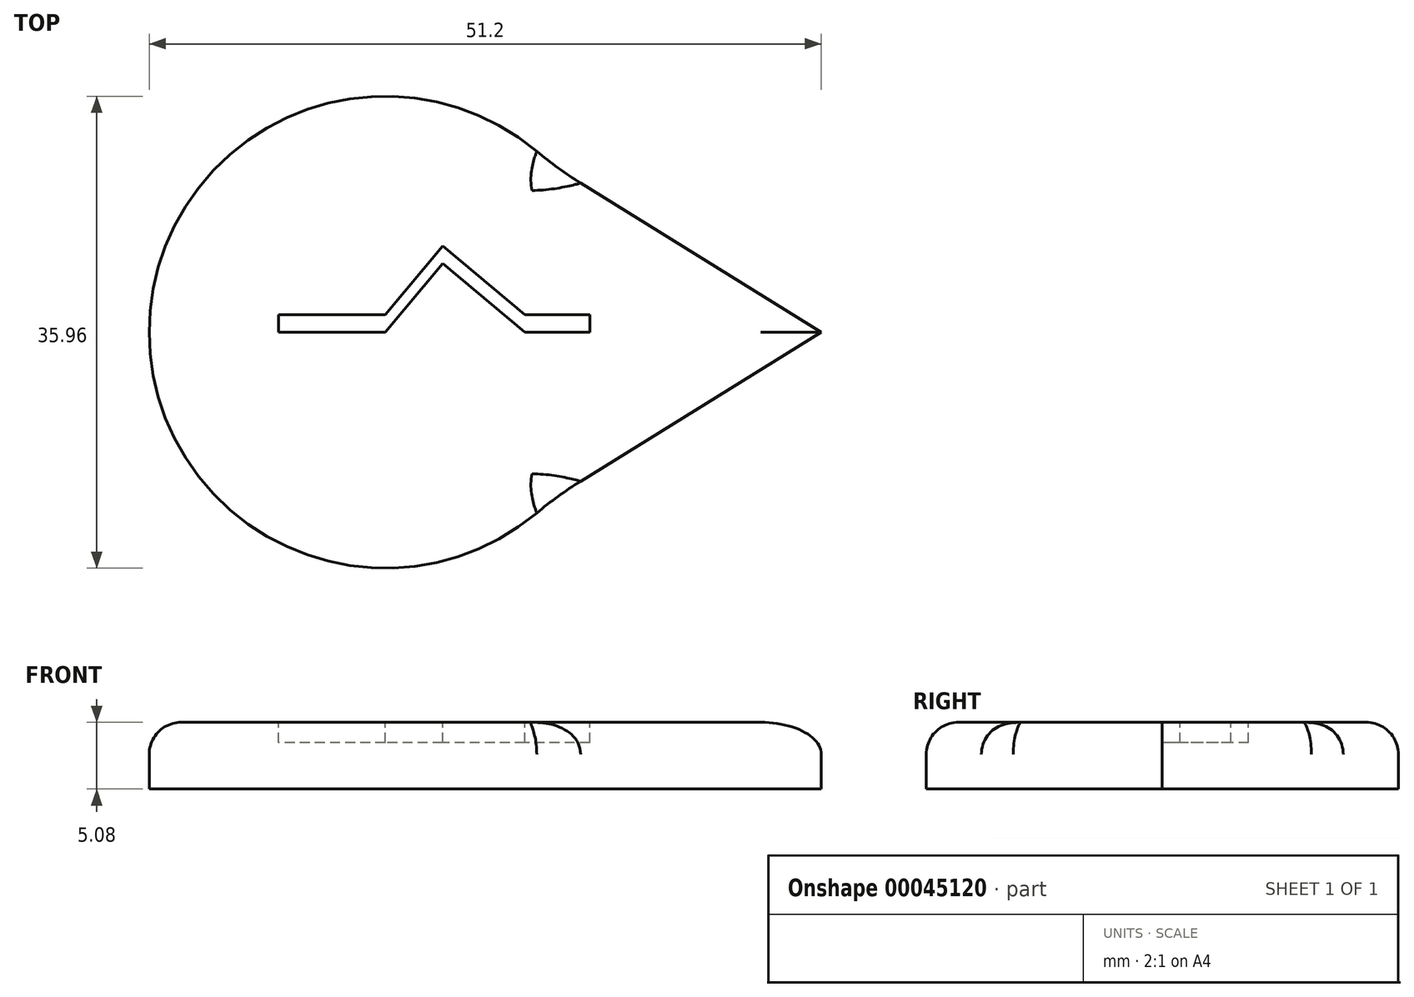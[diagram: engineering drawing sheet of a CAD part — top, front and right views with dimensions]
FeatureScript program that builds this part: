
annotation { "Feature Type Name" : "Feature", "Feature Type Description" : "" }
export const myFeature = defineFeature(function(context is Context, id is Id, definition is map)
    precondition{}
    {
        {
            var Q0;
            Q0=qCreatedBy(makeId("Top.planeOp"),FACE);
            var sketch = newSketch(context, id + "F0", { "sketchPlane" : qUnion([Q0])});
            skCircle(sketch, "E0", {"center": v(0, 0) * mm, "radius": 17.98 * mm});
            skLineSegment(sketch, "E1", {"start": v(-17.98, 0) * mm, "end": v(17.98, 0) * mm});
            skLineSegment(sketch, "E2", {"start": v(0, 0) * mm, "end": v(12.71, 12.71) * mm});
            skLineSegment(sketch, "E3", {"start": v(0, 0) * mm, "end": v(12.71, -12.71) * mm});
            skLineSegment(sketch, "E4", {"start": v(17.98, 0) * mm, "end": v(33.22, 0) * mm});
            skLineSegment(sketch, "E5", {"start": v(12.71, 12.71) * mm, "end": v(33.22, 0) * mm});
            skLineSegment(sketch, "E6", {"start": v(12.71, -12.71) * mm, "end": v(33.22, 0) * mm});
            skSolve(sketch);
        }
        {
            var Q0;
            Q0 = qSketchRegion(id + "F0", true);
            extrude(context, id + "F1", {"entities" : qUnion([Q0]), "depth" : 5.08 * mm});
        }
        {
            var Q0;
            Q0=makeQuery(id+"F1.opExtrude","CAP_EDGE",EDGE,{"disambiguationData":[OSD([sQuery(id+"F0.wireOp",EDGE,"E0")])],"isStart":false});
            var Q1;
            Q1=makeQuery(id+"F1.opExtrude","CAP_EDGE",EDGE,{"disambiguationData":[OSD([sQuery(id+"F0.wireOp",EDGE,"E6")])],"isStart":false});
            var Q2;
            Q2=makeQuery(id+"F1.opExtrude","CAP_EDGE",EDGE,{"disambiguationData":[OSD([sQuery(id+"F0.wireOp",EDGE,"E5")])],"isStart":false});
            fillet(context, id + "F2", {"entities" : qUnion([Q0, Q1, Q2]), "radius" : 2.43 * mm, "tangentPropagation" : true, "allowEdgeOverflow" : false});
        }
        {
            var Q0;
            Q0=makeQuery(id+"F1.opExtrude","SWEPT_EDGE",EDGE,{"disambiguationData":[OSD([sQuery(id+"F0.wireOp",EDGE,"E0"),sQuery(id+"F0.wireOp",EDGE,"E3"),sQuery(id+"F0.wireOp",EDGE,"E6")])]});
            var Q1;
            Q1=makeQuery(id+"F2.opFillet","BLEND_EDGE",EDGE,{"blendedFrom":[makeQuery(id+"F1.opExtrude","CAP_EDGE",EDGE,{"disambiguationData":[OSD([sQuery(id+"F0.wireOp",EDGE,"E0")])],"isStart":false}),makeQuery(id+"F1.opExtrude","CAP_EDGE",EDGE,{"disambiguationData":[OSD([sQuery(id+"F0.wireOp",EDGE,"E6")])],"isStart":false})],"blendedInto":[]});
            var Q2;
            Q2=makeQuery(id+"F1.opExtrude","SWEPT_EDGE",EDGE,{"disambiguationData":[OSD([sQuery(id+"F0.wireOp",EDGE,"E0"),sQuery(id+"F0.wireOp",EDGE,"E2"),sQuery(id+"F0.wireOp",EDGE,"E5")])]});
            var Q3;
            Q3=makeQuery(id+"F2.opFillet","BLEND_EDGE",EDGE,{"blendedFrom":[makeQuery(id+"F1.opExtrude","CAP_EDGE",EDGE,{"disambiguationData":[OSD([sQuery(id+"F0.wireOp",EDGE,"E0")])],"isStart":false}),makeQuery(id+"F1.opExtrude","CAP_EDGE",EDGE,{"disambiguationData":[OSD([sQuery(id+"F0.wireOp",EDGE,"E5")])],"isStart":false})],"blendedInto":[]});
            fillet(context, id + "F3", {"entities" : qUnion([Q0, Q1, Q2, Q3]), "radius" : 29.01 * mm, "tangentPropagation" : true, "allowEdgeOverflow" : false});
        }
        {
            var Q0;
            Q0=makeQuery(id+"F1.opExtrude","CAP_FACE",FACE,{"disambiguationData":[OSD([sQuery(id+"F0.wireOp",EDGE,"E0"),sQuery(id+"F0.wireOp",EDGE,"E5"),sQuery(id+"F0.wireOp",EDGE,"E6")])],"isStart":false});
            var sketch = newSketch(context, id + "F4", { "sketchPlane" : qUnion([Q0])});
            skLineSegment(sketch, "E7", {"start": v(0, 0) * mm, "end": v(-8.12, 0) * mm});
            skLineSegment(sketch, "E8", {"start": v(-8.12, 0) * mm, "end": v(-8.12, 1.33) * mm});
            skLineSegment(sketch, "E9", {"start": v(-8.12, 1.33) * mm, "end": v(0, 1.33) * mm});
            skLineSegment(sketch, "E10", {"start": v(0, 1.33) * mm, "end": v(4.37, 6.57) * mm});
            skLineSegment(sketch, "E11", {"start": v(4.37, 6.57) * mm, "end": v(10.64, 1.33) * mm});
            skLineSegment(sketch, "E12", {"start": v(10.64, 1.33) * mm, "end": v(15.57, 1.33) * mm});
            skLineSegment(sketch, "E13", {"start": v(15.57, 1.33) * mm, "end": v(15.57, 0) * mm});
            skLineSegment(sketch, "E14", {"start": v(15.57, 0) * mm, "end": v(10.64, 0) * mm});
            skLineSegment(sketch, "E15", {"start": v(10.64, 0) * mm, "end": v(4.37, 5.23) * mm});
            skLineSegment(sketch, "E16", {"start": v(4.37, 5.23) * mm, "end": v(0, 0) * mm});
            skSolve(sketch);
        }
        {
            var Q0;
            Q0=makeQuery(id+"F4.imprint","IMPRINT",FACE,{"disambiguationData":[TD([[makeQuery(id+"F4.imprint","IMPRINT",EDGE,{"derivedFrom":sQuery(id+"F4.wireOp",EDGE,"E7")}),-1.0]])]});
            extrude(context, id + "F5", {"entities" : qUnion([Q0]), "operationType" : NewBodyOperationType.REMOVE, "oppositeDirection" : true, "depth" : 1.55 * mm});
        }
    });
